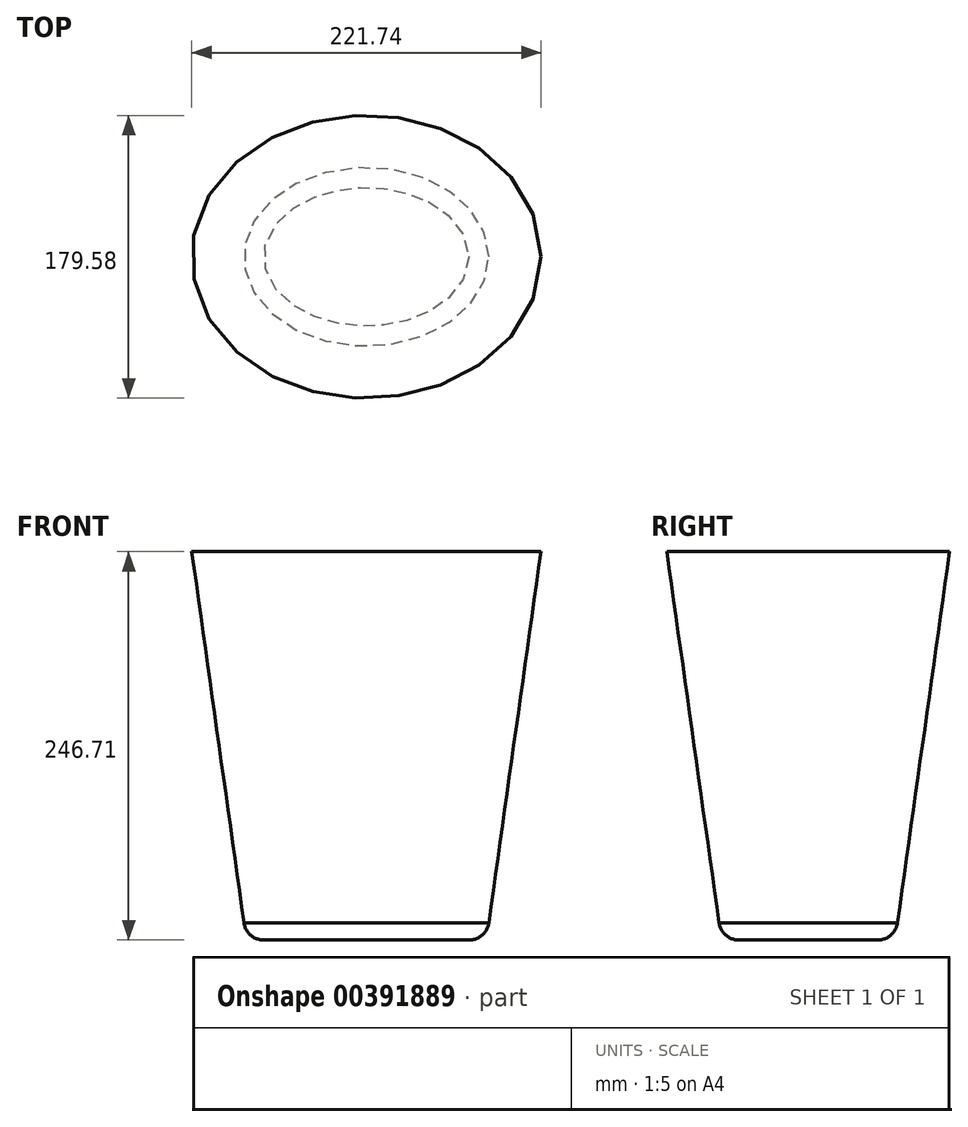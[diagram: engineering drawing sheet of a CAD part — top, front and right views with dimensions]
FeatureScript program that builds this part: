
annotation { "Feature Type Name" : "Feature", "Feature Type Description" : "" }
export const myFeature = defineFeature(function(context is Context, id is Id, definition is map)
    precondition{}
    {
        {
            var Q0;
            Q0=qCreatedBy(makeId("Top.planeOp"),FACE);
            var sketch = newSketch(context, id + "F0", { "sketchPlane" : qUnion([Q0])});
            skEllipse(sketch, "E0", {"center": v(0, 0) * mm, "majorRadius": 76.2 * mm, "minorRadius": 55.12 * mm, "majorAxis": v(-1, 0)});
            skSolve(sketch);
        }
        {
            var Q0;
            Q0=makeQuery(id+"F0.imprint","IMPRINT",FACE,{"disambiguationData":[TD([[makeQuery(id+"F0.imprint","IMPRINT",EDGE,{"derivedFrom":sQuery(id+"F0.wireOp",EDGE,"E0")}),1.0]])]});
            var Q1;
            Q1=sQuery(id+"F0.wireOp",EDGE,"E0");
            extrude(context, id + "F1", {"entities" : qUnion([Q0]), "surfaceEntities" : qUnion([Q1]), "depth" : 246.71 * mm, "hasDraft" : true, "draftAngle" : 8 * degree});
        }
        {
            var Q0;
            Q0=makeQuery(id+"F1.opExtrude","CAP_EDGE",EDGE,{"disambiguationData":[OSD([sQuery(id+"F0.wireOp",EDGE,"E0")])],"isStart":true});
            fillet(context, id + "F2", {"entities" : qUnion([Q0]), "radius" : 12.7 * mm, "tangentPropagation" : true, "allowEdgeOverflow" : false});
        }
    });
